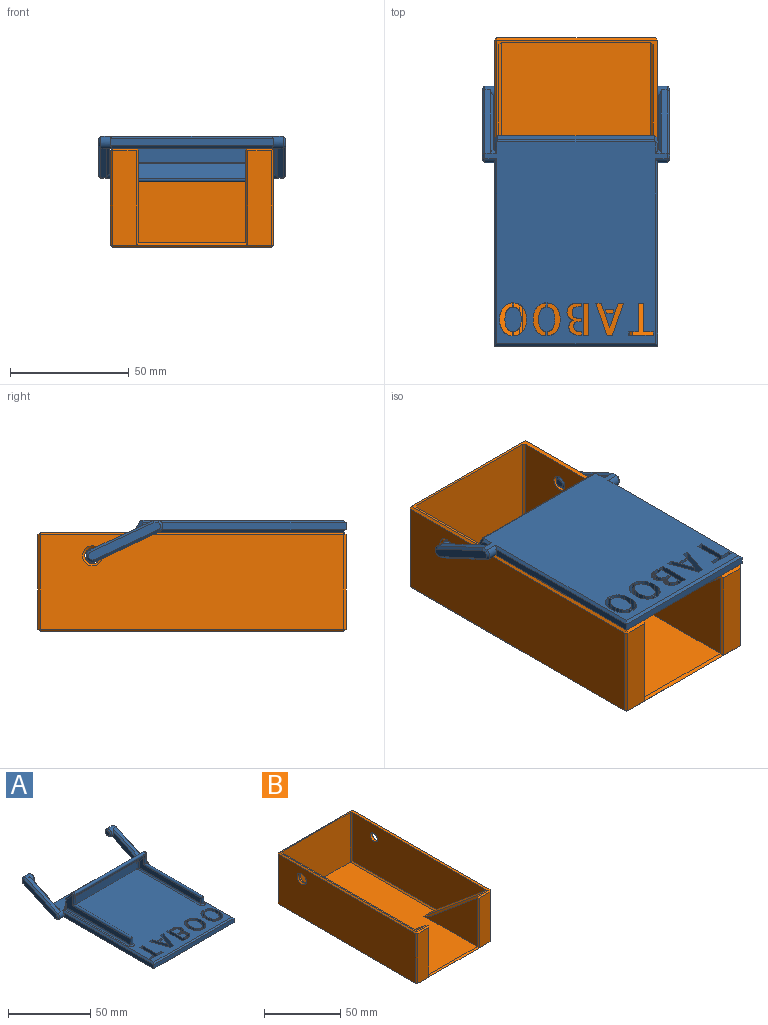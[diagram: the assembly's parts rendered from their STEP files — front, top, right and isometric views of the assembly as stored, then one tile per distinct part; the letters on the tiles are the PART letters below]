
ASSEMBLY  parts=2 mates=1
PART A: 227 faces, bbox 79.2x109.8x19.4 mm
  f0: plane 86.85x72mm, normal (0,0,1), area 4890.7mm2, adj f3,f5,f10,f15,f17,f20,f25,f34
  f1: plane 85.12x77mm, normal (0,0,-1), area 5413.3mm2, adj f9,f10,f15,f19,f20,f25,f73,f78
  f2: plane 3.11x2mm, normal (0,-1,0), area 1.3mm2, adj f57,f62,f64
  f3: plane 57x5.91mm, normal (0,-1,0), area 336.8mm2, adj f0,f48,f49,f50
  f4: plane 57x6.06mm, normal (0,-0.77,-0.64), area 450.8mm2, adj f49,f60,f61,f62
  f5: plane 6.59x4mm, normal (-1,0,0), area 16.7mm2, adj f0,f15,f85,f225
  f6: plane 66x3mm, normal (0,0.87,-0.5), area 228.6mm2, adj f81,f86,f225,f226
  f7: plane 69x3mm, normal (0,-1,0), area 207mm2, adj f8,f18,f84,f89
  f8: plane 77.78x3mm, normal (-1,0,0), area 232.5mm2, adj f7,f10,f83,f88
  f9: plane 26.81x12.5mm, normal (0,0.42,-0.91), area 73.9mm2, adj f1,f12,f67,f76
  f10: cylinder r=2.76mm len=5mm, axis (1,0,0), area 26.6mm2, adj f0,f1,f8,f11,f80,f83,f88
  f11: plane 26.81x12.5mm, normal (0,-0.42,0.91), area 73.9mm2, adj f10,f12,f69,f79
  f12: cylinder r=2.76mm len=5.52mm, axis (1,0,0), area 59.5mm2, adj f9,f11,f16,f66,f67,f69,f77
  f13: plane 30.32x15.76mm, normal (-1,0,0), area 113.4mm2, adj f76,f77,f78,f79,f80
  f14: plane 3.52x3.52mm, normal (1,0,0), area 9.7mm2, adj f66
  f15: cylinder r=2.76mm len=5mm, axis (1,0,0), area 5.6mm2, adj f0,f1,f5,f16,f67,f69,f85
  f16: plane 24.44x13.89mm, normal (1,0,0), area 86mm2, adj f12,f15,f67,f69
  f17: plane 6.59x4mm, normal (1,0,0), area 16.7mm2, adj f0,f25,f87,f226
  f18: plane 77.78x3mm, normal (1,0,0), area 232.5mm2, adj f7,f20,f82,f90
  f19: plane 26.81x12.5mm, normal (0,0.42,-0.91), area 73.9mm2, adj f1,f22,f68,f71
  f20: cylinder r=2.76mm len=5mm, axis (-1,0,0), area 26.6mm2, adj f0,f1,f18,f21,f75,f82,f90
  f21: plane 26.81x12.5mm, normal (0,-0.42,0.91), area 73.9mm2, adj f20,f22,f70,f74
  f22: cylinder r=2.76mm len=5.52mm, axis (-1,0,0), area 59.5mm2, adj f19,f21,f26,f65,f68,f70,f72
  f23: plane 30.32x15.76mm, normal (1,0,0), area 113.4mm2, adj f71,f72,f73,f74,f75
  f24: plane 3.52x3.52mm, normal (-1,0,0), area 9.7mm2, adj f65
  f25: cylinder r=2.76mm len=5mm, axis (-1,0,0), area 5.6mm2, adj f0,f1,f17,f26,f68,f70,f87
  f26: plane 24.44x13.89mm, normal (-1,0,0), area 86mm2, adj f22,f25,f68,f70
  f27: plane 55x12.25mm, normal (1,0,0), area 247.5mm2, adj f36,f41,f46,f47,f53,f54
  f28: plane 61x6mm, normal (0,1,0), area 366mm2, adj f33,f35,f45,f46
  f29: plane 55x12.25mm, normal (-1,0,0), area 247.5mm2, adj f34,f44,f45,f51,f52,f57
  f30: plane 53x9.14mm, normal (1,0,0), area 222.7mm2, adj f43,f44,f50,f51,f57,f61
  f31: plane 53x9.14mm, normal (-1,0,0), area 222.7mm2, adj f41,f42,f47,f48,f54,f60
  f32: plane 3.11x2mm, normal (0,-1,0), area 1.3mm2, adj f54,f62,f63
  f33: plane 61x6.9mm, normal (0,0.77,0.64), area 549.1mm2, adj f28,f52,f53,f62
  f34: cylinder r=1mm len=55mm, axis (0,-1,0), area 86.4mm2, adj f0,f29,f38,f39
  f35: cylinder r=1mm len=61mm, axis (-1,0,0), area 95.8mm2, adj f0,f28,f39,f40
  f36: cylinder r=1mm len=55mm, axis (0,1,0), area 86.4mm2, adj f0,f27,f37,f40
  f37: torus R=2mm, axis (0,0,1), area 6.7mm2, adj f0,f36,f41,f42
  f38: torus R=2mm, axis (0,0,1), area 6.7mm2, adj f0,f34,f43,f44
  f39: torus R=2mm, axis (0,0,1), area 3.4mm2, adj f0,f34,f35,f45
  f40: torus R=2mm, axis (0,0,1), area 3.4mm2, adj f0,f35,f36,f46
  f41: cylinder r=1mm len=5mm, axis (0,0,-1), area 14.6mm2, adj f27,f31,f37,f47
  f42: cylinder r=1mm len=54mm, axis (0,-1,0), area 84.3mm2, adj f0,f31,f37,f48
  f43: cylinder r=1mm len=54mm, axis (0,1,0), area 84.3mm2, adj f0,f30,f38,f50
  f44: cylinder r=1mm len=5mm, axis (0,0,-1), area 14.6mm2, adj f29,f30,f38,f51
  f45: cylinder r=1mm len=6mm, axis (0,0,-1), area 9.1mm2, adj f28,f29,f39,f52
  f46: cylinder r=1mm len=6mm, axis (0,0,-1), area 9.1mm2, adj f27,f28,f40,f53
  f47: cylinder r=1mm len=50.45mm, axis (0,-1,0), area 155.3mm2, adj f27,f31,f41,f54
  f48: cylinder r=1mm len=5.91mm, axis (0,0,1), area 8.7mm2, adj f3,f31,f42,f55
  f49: cylinder r=1mm len=57mm, axis (1,0,0), area 39.8mm2, adj f3,f4,f55,f56
  f50: cylinder r=1mm len=5.91mm, axis (0,0,1), area 8.7mm2, adj f3,f30,f43,f56
  f51: cylinder r=1mm len=50.45mm, axis (0,1,0), area 155.3mm2, adj f29,f30,f44,f57
  f52: cylinder r=1mm len=7.54mm, axis (0,-0.64,0.77), area 13.9mm2, adj f29,f33,f45,f58
  f53: cylinder r=1mm len=7.54mm, axis (0,0.64,-0.77), area 13.9mm2, adj f27,f33,f46,f59
  f54: cylinder r=1mm len=8.25mm, axis (0,0,1), area 19mm2, adj f27,f31,f32,f47,f59,f63
  f55: sphere r=1mm, area 0.8mm2, adj f48,f49,f60
  f56: sphere r=1mm, area 0.8mm2, adj f49,f50,f61
  f57: cylinder r=1mm len=8.25mm, axis (0,0,-1), area 19mm2, adj f2,f29,f30,f51,f58,f64
  f58: sphere r=1mm, area 2.4mm2, adj f52,f57,f62
  f59: sphere r=1mm, area 2.4mm2, adj f53,f54,f62
  f60: cylinder r=1mm len=6.7mm, axis (0,0.64,-0.77), area 11.1mm2, adj f4,f31,f55,f63
  f61: cylinder r=1mm len=6.7mm, axis (0,0.64,-0.77), area 11.1mm2, adj f4,f30,f56,f64
  f62: cylinder r=1mm len=61mm, axis (-1,0,0), area 188.8mm2, adj f2,f4,f32,f33,f58,f59,f63,f64
  f63: bspline ~3.65x2.35mm, area 3.7mm2, adj f32,f54,f60,f62
  f64: bspline ~3.65x2.35mm, area 3.7mm2, adj f2,f57,f61,f62
  f65: cone r=2.76mm half-angle=45deg, axis (1,0,0), area 20.1mm2, adj f22,f24
  f66: cone r=1.76mm half-angle=45deg, axis (-1,0,0), area 20.1mm2, adj f12,f14
  f67: plane 26.81x12.51mm, normal (0.71,0.3,-0.64), area 37.6mm2, adj f9,f12,f15,f16
  f68: plane 26.81x12.51mm, normal (-0.71,0.3,-0.64), area 37.6mm2, adj f19,f22,f25,f26
  f69: plane 26.81x12.51mm, normal (0.71,-0.3,0.64), area 38.2mm2, adj f0,f11,f12,f15,f16
  f70: plane 26.84x12.54mm, normal (-0.71,-0.3,0.64), area 38.2mm2, adj f0,f21,f22,f25,f26
  f71: plane 27.03x13.41mm, normal (0.71,0.3,-0.64), area 41.7mm2, adj f19,f23,f72,f73
  f72: cone r=2.76mm half-angle=45deg, axis (-1,0,0), area 10mm2, adj f22,f23,f71,f74
  f73: plane 2.37x1.04mm, normal (0.71,0,-0.71), area 3mm2, adj f1,f23,f71,f75
  f74: plane 27.23x13.41mm, normal (0.71,-0.3,0.64), area 41.8mm2, adj f21,f23,f72,f75
  f75: cone r=2.76mm half-angle=45deg, axis (-1,0,0), area 7.1mm2, adj f20,f23,f73,f74
  f76: plane 27.03x13.41mm, normal (-0.71,0.3,-0.64), area 41.7mm2, adj f9,f13,f77,f78
  f77: cone r=1.76mm half-angle=45deg, axis (1,0,0), area 10mm2, adj f12,f13,f76,f79
  f78: plane 2.37x1.04mm, normal (-0.71,0,-0.71), area 3mm2, adj f1,f13,f76,f80
  f79: plane 27.23x13.41mm, normal (-0.71,-0.3,0.64), area 41.8mm2, adj f11,f13,f77,f80
  f80: cone r=1.76mm half-angle=45deg, axis (1,0,0), area 7.1mm2, adj f10,f13,f78,f79
  f81: plane 69x1.5mm, normal (0,0.87,0.5), area 116.9mm2, adj f0,f6,f225,f226
  f82: plane 79.1x1.16mm, normal (0.71,0,0.71), area 110mm2, adj f0,f18,f20,f84
  f83: plane 79.1x1.16mm, normal (-0.71,0,0.71), area 110mm2, adj f0,f8,f10,f84
  f84: plane 69x1mm, normal (0,-0.71,0.71), area 96.2mm2, adj f0,f7,f82,f83
  f85: plane 4.86x1mm, normal (-0.71,0,-0.71), area 5.5mm2, adj f1,f5,f15,f225
  f86: plane 67x0.87mm, normal (0,0.5,-0.87), area 66.5mm2, adj f1,f6,f225,f226
  f87: plane 4.86x1mm, normal (0.71,0,-0.71), area 5.5mm2, adj f1,f17,f25,f226
  f88: plane 79.1x1.16mm, normal (-0.71,0,-0.71), area 110mm2, adj f1,f8,f10,f89
  f89: plane 69x1mm, normal (0,-0.71,-0.71), area 96.2mm2, adj f1,f7,f88,f90
  f90: plane 79.1x1.16mm, normal (0.71,0,-0.71), area 110mm2, adj f1,f18,f20,f89
  f91: extruded ~5x2.1mm, area 10.9mm2, adj f0,f1,f92,f108
  f92: plane 5x1.83mm, normal (1,0,0), area 9.2mm2, adj f0,f1,f91,f93
  f93: extruded ~5x1.17mm, area 6.2mm2, adj f0,f1,f92,f94
  f94: extruded ~5x0.97mm, area 6.8mm2, adj f0,f1,f93,f95
  f95: extruded ~5x1.55mm, area 8.5mm2, adj f0,f1,f94,f96
  f96: extruded ~5x2.25mm, area 11.3mm2, adj f0,f1,f95,f97
  f97: extruded ~5x2.25mm, area 11.3mm2, adj f0,f1,f96,f98
  f98: extruded ~5x1.55mm, area 8.5mm2, adj f0,f1,f97,f99
  f99: extruded ~5x0.96mm, area 6.8mm2, adj f0,f1,f98,f100
  f100: extruded ~5x1.19mm, area 6.3mm2, adj f0,f1,f99,f101
  f101: plane 5x1.83mm, normal (1,0,0), area 9.2mm2, adj f0,f1,f100,f102
  f102: extruded ~5x2.11mm, area 11mm2, adj f0,f1,f101,f103
  f103: extruded ~5x1.67mm, area 10.8mm2, adj f0,f1,f102,f104
  f104: extruded ~5x2.16mm, area 12.2mm2, adj f0,f1,f103,f105
  f105: extruded ~5x2.92mm, area 14.8mm2, adj f0,f1,f104,f106
  f106: extruded ~5x2.92mm, area 14.8mm2, adj f0,f1,f105,f107
  f107: extruded ~5x2.15mm, area 12.2mm2, adj f0,f1,f106,f108
  f108: extruded ~5x1.68mm, area 10.9mm2, adj f0,f1,f91,f107
  f109: extruded ~5x2.92mm, area 14.8mm2, adj f0,f1,f110,f126
  f110: extruded ~5x2.92mm, area 14.8mm2, adj f0,f1,f109,f111
  f111: extruded ~5x2.16mm, area 12.2mm2, adj f0,f1,f110,f112
  f112: extruded ~5x1.69mm, area 10.9mm2, adj f0,f1,f111,f113
  f113: extruded ~5x2.11mm, area 11mm2, adj f0,f1,f112,f114
  f114: plane 5x1.83mm, normal (-1,0,0), area 9.2mm2, adj f0,f1,f113,f115
  f115: extruded ~5x1.17mm, area 6.2mm2, adj f0,f1,f114,f116
  f116: extruded ~5x0.97mm, area 6.9mm2, adj f0,f1,f115,f117
  f117: extruded ~5x1.56mm, area 8.5mm2, adj f0,f1,f116,f118
  f118: extruded ~5x2.25mm, area 11.3mm2, adj f0,f1,f117,f119
  f119: extruded ~5x2.24mm, area 11.3mm2, adj f0,f1,f118,f120
  f120: extruded ~5x1.55mm, area 8.5mm2, adj f0,f1,f119,f121
  f121: extruded ~5x0.96mm, area 6.7mm2, adj f0,f1,f120,f122
  f122: extruded ~5x1.18mm, area 6.3mm2, adj f0,f1,f121,f123
  f123: plane 5x1.85mm, normal (-1,0,0), area 9.3mm2, adj f0,f1,f122,f124
  f124: extruded ~5x2.12mm, area 11mm2, adj f0,f1,f123,f125
  f125: extruded ~5x1.68mm, area 10.9mm2, adj f0,f1,f124,f126
  f126: extruded ~5x2.15mm, area 12.2mm2, adj f0,f1,f109,f125
  f127: extruded ~5x2.1mm, area 10.9mm2, adj f0,f1,f128,f144
  f128: plane 5x1.83mm, normal (1,0,0), area 9.2mm2, adj f0,f1,f127,f129
  f129: extruded ~5x1.17mm, area 6.2mm2, adj f0,f1,f128,f130
  f130: extruded ~5x0.97mm, area 6.8mm2, adj f0,f1,f129,f131
  f131: extruded ~5x1.55mm, area 8.5mm2, adj f0,f1,f130,f132
  f132: extruded ~5x2.25mm, area 11.3mm2, adj f0,f1,f131,f133
  f133: extruded ~5x2.25mm, area 11.3mm2, adj f0,f1,f132,f134
  f134: extruded ~5x1.55mm, area 8.5mm2, adj f0,f1,f133,f135
  f135: extruded ~5x0.96mm, area 6.8mm2, adj f0,f1,f134,f136
  f136: extruded ~5x1.19mm, area 6.3mm2, adj f0,f1,f135,f137
  f137: plane 5x1.83mm, normal (1,0,0), area 9.2mm2, adj f0,f1,f136,f138
  f138: extruded ~5x2.11mm, area 11mm2, adj f0,f1,f137,f139
  f139: extruded ~5x1.67mm, area 10.8mm2, adj f0,f1,f138,f140
  f140: extruded ~5x2.16mm, area 12.2mm2, adj f0,f1,f139,f141
  f141: extruded ~5x2.92mm, area 14.8mm2, adj f0,f1,f140,f142
  f142: extruded ~5x2.92mm, area 14.8mm2, adj f0,f1,f141,f143
  f143: extruded ~5x2.15mm, area 12.2mm2, adj f0,f1,f142,f144
  f144: extruded ~5x1.68mm, area 10.9mm2, adj f0,f1,f127,f143
  f145: extruded ~5x2.92mm, area 14.8mm2, adj f0,f1,f146,f162
  f146: extruded ~5x2.92mm, area 14.8mm2, adj f0,f1,f145,f147
  f147: extruded ~5x2.16mm, area 12.2mm2, adj f0,f1,f146,f148
  f148: extruded ~5x1.69mm, area 10.9mm2, adj f0,f1,f147,f149
  f149: extruded ~5x2.11mm, area 11mm2, adj f0,f1,f148,f150
  f150: plane 5x1.83mm, normal (-1,0,0), area 9.2mm2, adj f0,f1,f149,f151
  f151: extruded ~5x1.17mm, area 6.2mm2, adj f0,f1,f150,f152
  f152: extruded ~5x0.97mm, area 6.9mm2, adj f0,f1,f151,f153
  f153: extruded ~5x1.56mm, area 8.5mm2, adj f0,f1,f152,f154
  f154: extruded ~5x2.25mm, area 11.3mm2, adj f0,f1,f153,f155
  f155: extruded ~5x2.24mm, area 11.3mm2, adj f0,f1,f154,f156
  f156: extruded ~5x1.55mm, area 8.5mm2, adj f0,f1,f155,f157
  f157: extruded ~5x0.96mm, area 6.7mm2, adj f0,f1,f156,f158
  f158: extruded ~5x1.18mm, area 6.3mm2, adj f0,f1,f157,f159
  f159: plane 5x1.85mm, normal (-1,0,0), area 9.3mm2, adj f0,f1,f158,f160
  f160: extruded ~5x2.12mm, area 11mm2, adj f0,f1,f159,f161
  f161: extruded ~5x1.68mm, area 10.9mm2, adj f0,f1,f160,f162
  f162: extruded ~5x2.15mm, area 12.2mm2, adj f0,f1,f145,f161
  f163: plane 5x2.22mm, normal (0,1,0), area 11.1mm2, adj f0,f1,f164,f166
  f164: plane 13.64x5mm, normal (1,0,0), area 68.2mm2, adj f0,f1,f163,f165
  f165: plane 5x2.22mm, normal (0,-1,0), area 11.1mm2, adj f0,f1,f164,f166
  f166: plane 13.64x5mm, normal (-1,0,0), area 68.2mm2, adj f0,f1,f163,f165
  f167: extruded ~5x0.91mm, area 4.8mm2, adj f0,f1,f168,f205
  f168: extruded ~5x0.69mm, area 3.8mm2, adj f0,f1,f167,f169
  f169: extruded ~5x0.64mm, area 4.3mm2, adj f0,f1,f168,f170
  f170: extruded ~5x0.82mm, area 4.7mm2, adj f0,f1,f169,f171
  f171: extruded ~5x1.04mm, area 5.3mm2, adj f0,f1,f170,f172
  f172: extruded ~5x1.7mm, area 8.8mm2, adj f0,f1,f171,f173
  f173: extruded ~5x1.16mm, area 7.7mm2, adj f0,f1,f172,f174
  f174: extruded ~5x1.44mm, area 8mm2, adj f0,f1,f173,f175
  f175: extruded ~5x1.68mm, area 8.5mm2, adj f0,f1,f174,f176
  f176: plane 5x0.94mm, normal (0,1,0), area 4.7mm2, adj f0,f1,f175,f177
  f177: plane 5x1.68mm, normal (1,0,0), area 8.4mm2, adj f0,f1,f176,f178
  f178: plane 5x0.72mm, normal (0,-1,0), area 3.6mm2, adj f0,f1,f177,f179
  f179: extruded ~5x1.37mm, area 6.9mm2, adj f0,f1,f178,f180
  f180: extruded ~5x0.8mm, area 4.7mm2, adj f0,f1,f179,f181
  f181: extruded ~5x0.66mm, area 3.8mm2, adj f0,f1,f180,f182
  f182: extruded ~5x0.7mm, area 3.5mm2, adj f0,f1,f181,f183
  f183: extruded ~5x1.28mm, area 6.5mm2, adj f0,f1,f182,f184
  f184: extruded ~5x0.63mm, area 4.4mm2, adj f0,f1,f183,f185
  f185: extruded ~5x0.8mm, area 4.1mm2, adj f0,f1,f184,f186
  f186: extruded ~5x0.83mm, area 4.2mm2, adj f0,f1,f185,f187
  f187: plane 5x0.89mm, normal (0,1,0), area 4.4mm2, adj f0,f1,f186,f188
  f188: plane 5x1.5mm, normal (1,0,0), area 7.5mm2, adj f0,f1,f187,f189
  f189: plane 5x1.85mm, normal (0,-1,0), area 9.3mm2, adj f0,f1,f188,f190
  f190: extruded ~5x1.68mm, area 9.4mm2, adj f0,f1,f189,f191
  f191: extruded ~5x1.68mm, area 9.1mm2, adj f0,f1,f190,f192
  f192: extruded ~5x1.68mm, area 9.1mm2, adj f0,f1,f191,f193
  f193: extruded ~5x1.54mm, area 8.6mm2, adj f0,f1,f192,f194
  f194: plane 5x2.02mm, normal (0,1,0), area 10.1mm2, adj f0,f1,f193,f195
  f195: plane 5x1.63mm, normal (1,0,0), area 8.1mm2, adj f0,f1,f194,f196
  f196: plane 5x2.15mm, normal (0,-1,0), area 10.7mm2, adj f0,f1,f195,f197
  f197: extruded ~5x0.46mm, area 2.3mm2, adj f0,f1,f196,f198
  f198: extruded ~5x0.81mm, area 4.1mm2, adj f0,f1,f197,f199
  f199: extruded ~5x0.94mm, area 5.1mm2, adj f0,f1,f198,f200
  f200: extruded ~5x0.91mm, area 5.7mm2, adj f0,f1,f199,f201
  f201: extruded ~5x1.1mm, area 6.5mm2, adj f0,f1,f200,f202
  f202: extruded ~5x1.59mm, area 8.1mm2, adj f0,f1,f201,f203
  f203: extruded ~5x1.34mm, area 6.9mm2, adj f0,f1,f202,f204
  f204: extruded ~5x0.99mm, area 6.1mm2, adj f0,f1,f203,f205
  f205: extruded ~5x0.9mm, area 5.5mm2, adj f0,f1,f167,f204
  f206: plane 5x2.29mm, normal (0,-1,0), area 11.5mm2, adj f0,f1,f207,f212
  f207: plane 13.62x5mm, normal (-0.94,0.33,0), area 72.1mm2, adj f0,f1,f206,f208
  f208: plane 5x2.2mm, normal (0,1,0), area 11mm2, adj f0,f1,f207,f209
  f209: plane 13.62x5mm, normal (0.94,0.33,0), area 72.2mm2, adj f0,f1,f208,f210
  f210: plane 5x2.31mm, normal (0,-1,0), area 11.6mm2, adj f0,f1,f209,f211
  f211: plane 10.21x5mm, normal (-0.94,-0.33,0), area 54.1mm2, adj f0,f1,f210,f212
  f212: plane 10.21x5mm, normal (0.95,-0.33,0), area 54mm2, adj f0,f1,f206,f211
  f213: plane 5x1.5mm, normal (-0.94,0.34,0), area 8mm2, adj f0,f1,f214,f216
  f214: plane 5x2.48mm, normal (0,1,0), area 12.4mm2, adj f0,f1,f213,f215
  f215: plane 5x1.5mm, normal (0.95,0.33,0), area 7.9mm2, adj f0,f1,f214,f216
  f216: plane 5x3.54mm, normal (0,-1,0), area 17.7mm2, adj f0,f1,f213,f215
  f217: plane 5x1.52mm, normal (-1,0,0), area 7.6mm2, adj f0,f1,f218,f224
  f218: plane 10.38x5mm, normal (0,1,0), area 51.9mm2, adj f0,f1,f217,f219
  f219: plane 5x1.52mm, normal (1,0,0), area 7.6mm2, adj f0,f1,f218,f220
  f220: plane 5x4.07mm, normal (0,-1,0), area 20.4mm2, adj f0,f1,f219,f221
  f221: plane 12.12x5mm, normal (1,0,0), area 60.6mm2, adj f0,f1,f220,f222
  f222: plane 5x2.24mm, normal (0,-1,0), area 11.2mm2, adj f0,f1,f221,f223
  f223: plane 12.12x5mm, normal (-1,0,0), area 60.6mm2, adj f0,f1,f222,f224
  f224: plane 5x4.07mm, normal (0,-1,0), area 20.4mm2, adj f0,f1,f217,f223
  f225: plane 5x3.18mm, normal (-0.71,0.61,-0.35), area 9.4mm2, adj f5,f6,f81,f85,f86
  f226: plane 5x3.18mm, normal (0.71,0.61,-0.35), area 9.4mm2, adj f6,f17,f81,f86,f87
PART B: 47 faces, bbox 69x130x42 mm
  f0: plane 40x10mm, normal (0,-1,0), area 400mm2, adj f26,f28,f31,f32
  f1: plane 127x63mm, normal (0,0,1), area 7112.5mm2, adj f7,f10,f15,f18,f19,f21,f22,f25
  f2: plane 47.72x39.77mm, normal (0,0.64,0.77), area 527.6mm2, adj f6,f9,f21,f22,f45
  f3: plane 40x10mm, normal (0,-1,0), area 400mm2, adj f23,f24,f26,f27
  f4: plane 128x67mm, normal (0,0,-1), area 8576mm2, adj f26,f33,f34,f35
  f5: plane 67x40mm, normal (0,1,0), area 2680mm2, adj f34,f40,f41,f43
  f6: plane 128x68mm, normal (0,0,1), area 467.6mm2, adj f2,f7,f8,f9,f12,f14,f17,f20
  f7: plane 63x40mm, normal (0,-1,0), area 2520mm2, adj f1,f6,f17,f20
  f8: plane 128x41mm, normal (1,0,0), area 5214.6mm2, adj f6,f11,f27,f35,f41
  f9: plane 125x39mm, normal (-1,0,0), area 3929mm2, adj f2,f6,f11,f20,f21
  f10: plane 49.36x38.88mm, normal (-1,0,0), area 909.4mm2, adj f1,f22,f23,f45
  f11: cylinder r=3.26mm len=6.52mm, axis (1,0,0), area 40.9mm2, adj f8,f9
  f12: plane 47.72x39.77mm, normal (0,0.64,0.77), area 527.6mm2, adj f6,f14,f18,f19,f46
  f13: plane 128x40mm, normal (-1,0,0), area 5063mm2, adj f32,f33,f39,f40,f44
  f14: plane 125x39mm, normal (1,0,0), area 3929mm2, adj f6,f12,f16,f17,f18
  f15: plane 49.36x38.88mm, normal (1,0,0), area 909.4mm2, adj f1,f19,f28,f46
  f16: cylinder r=3.26mm len=6.52mm, axis (-1,0,0), area 20.5mm2, adj f14,f44
  f17: plane 40x1mm, normal (0.71,-0.71,0), area 55.9mm2, adj f6,f7,f14,f18
  f18: plane 79.2x1mm, normal (0.71,0,0.71), area 110.4mm2, adj f1,f12,f14,f17,f19
  f19: plane 9.23x4.78mm, normal (0,0.34,0.94), area 9.5mm2, adj f1,f12,f15,f18,f46
  f20: plane 40x1mm, normal (-0.71,-0.71,0), area 55.9mm2, adj f6,f7,f9,f21
  f21: plane 79.2x1mm, normal (-0.71,0,0.71), area 110.4mm2, adj f1,f2,f9,f20,f22
  f22: plane 9.23x4.78mm, normal (0,0.34,0.94), area 9.5mm2, adj f1,f2,f10,f21,f45
  f23: plane 40.64x1mm, normal (-0.71,-0.71,0), area 56.3mm2, adj f3,f10,f24,f25,f45
  f24: plane 11.64x1mm, normal (0,-0.71,0.71), area 15.3mm2, adj f3,f6,f23,f27,f45
  f25: plane 47x1mm, normal (0,-0.71,0.71), area 65.1mm2, adj f1,f23,f26,f28
  f26: plane 67x1mm, normal (0,-0.71,-0.71), area 94.8mm2, adj f0,f3,f4,f25,f29,f30
  f27: plane 41x1mm, normal (0.71,-0.71,0), area 57.3mm2, adj f3,f8,f24,f30
  f28: plane 40.64x1mm, normal (0.71,-0.71,0), area 56.3mm2, adj f0,f15,f25,f31,f46
  f29: plane 1x1mm, normal (-0.58,-0.58,-0.58), area 0.9mm2, adj f26,f32,f33
  f30: plane 1x1mm, normal (0.58,-0.58,-0.58), area 0.9mm2, adj f26,f27,f35
  f31: plane 10.64x1mm, normal (0,-0.71,0.71), area 14.6mm2, adj f0,f6,f28,f36,f46
  f32: plane 40x1mm, normal (-0.71,-0.71,0), area 56.6mm2, adj f0,f13,f29,f36
  f33: plane 128x1mm, normal (-0.71,0,-0.71), area 181mm2, adj f4,f13,f29,f37
  f34: plane 67x1mm, normal (0,0.71,-0.71), area 94.8mm2, adj f4,f5,f37,f38
  f35: plane 128x1mm, normal (0.71,0,-0.71), area 181mm2, adj f4,f8,f30,f38
  f36: plane 1x1mm, normal (-0.58,-0.58,0.58), area 0.9mm2, adj f31,f32,f39
  f37: plane 1x1mm, normal (-0.58,0.58,-0.58), area 0.9mm2, adj f33,f34,f40
  f38: plane 1x1mm, normal (0.58,0.58,-0.58), area 0.9mm2, adj f34,f35,f41
  f39: plane 128x1mm, normal (-0.71,0,0.71), area 181mm2, adj f6,f13,f36,f42
  f40: plane 40x1mm, normal (-0.71,0.71,0), area 56.6mm2, adj f5,f13,f37,f42
  f41: plane 41x1mm, normal (0.71,0.71,0), area 57.3mm2, adj f5,f8,f38,f43
  f42: plane 1x1mm, normal (-0.58,0.58,0.58), area 0.9mm2, adj f39,f40,f43
  f43: plane 68x1mm, normal (0,0.71,0.71), area 95.5mm2, adj f5,f6,f41,f42
  f44: cone r=4.26mm half-angle=45deg, axis (-1,0,0), area 33.4mm2, adj f13,f16
  f45: plane 49.08x39.77mm, normal (-0.71,0.45,0.54), area 128.5mm2, adj f2,f6,f10,f22,f23,f24
  f46: plane 49.08x39.77mm, normal (0.71,0.45,0.54), area 128.5mm2, adj f6,f12,f15,f19,f28,f31
PLACE A rot(axis=(0,-1,0),180deg) t=(-16.16,-20.49,43.46)mm
PLACE B t=(-16.25,-1.08,-1.54)mm fixed
MATE revolute A.f12 <-> B.f11  axis (-1,0,0) through (16.25,40.83,28.46)mm
